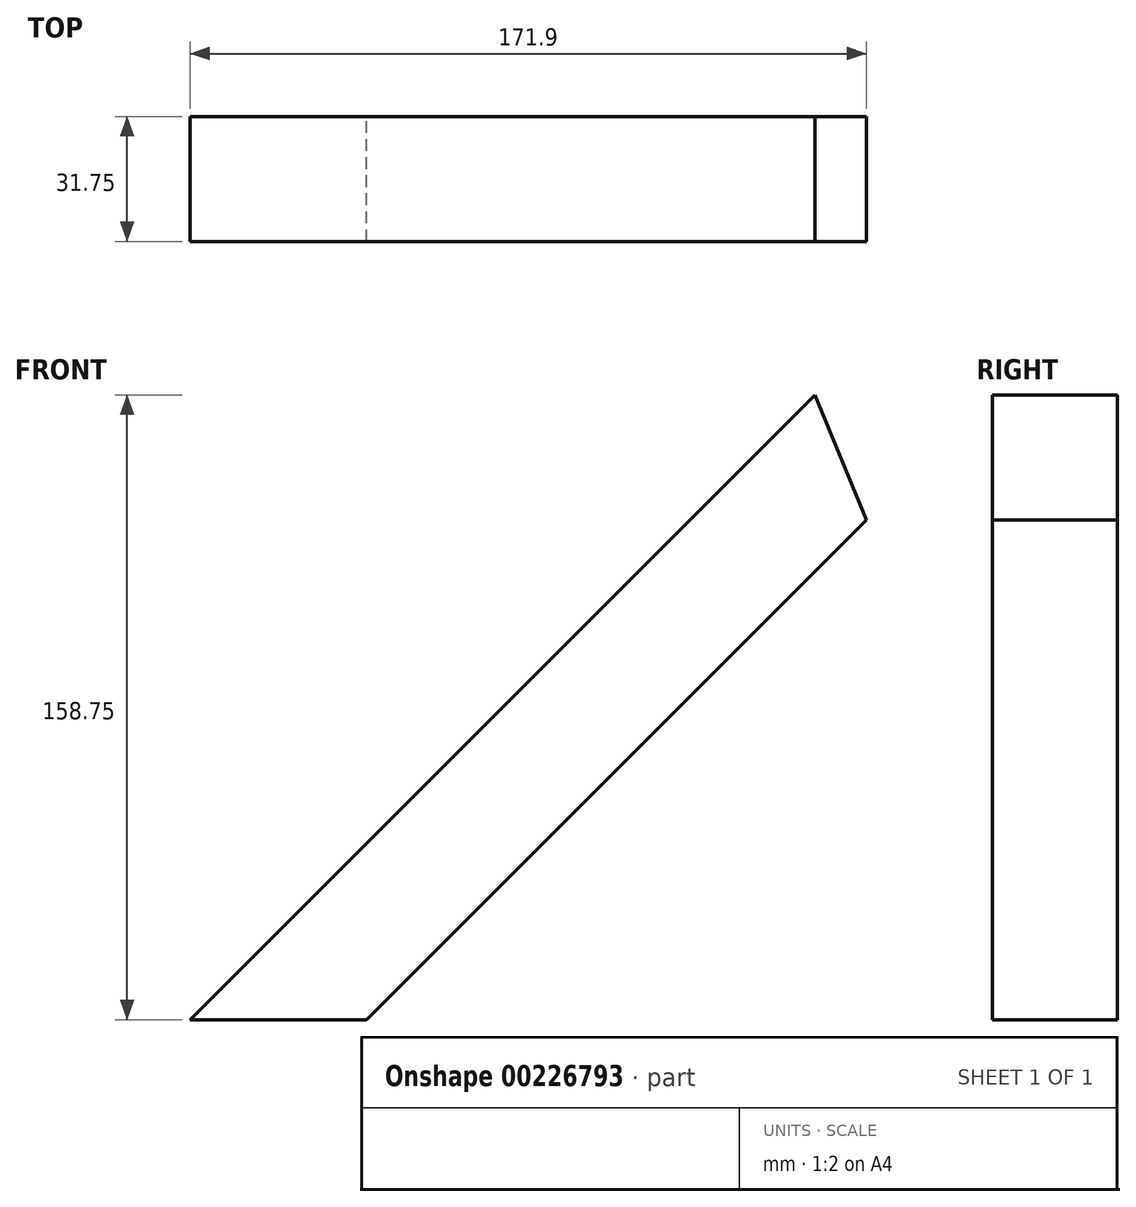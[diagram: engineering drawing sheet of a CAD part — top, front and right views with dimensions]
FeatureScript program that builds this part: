
annotation { "Feature Type Name" : "Feature", "Feature Type Description" : "" }
export const myFeature = defineFeature(function(context is Context, id is Id, definition is map)
    precondition{}
    {
        {
            var Q0;
            Q0=qCreatedBy(makeId("Front.planeOp"),FACE);
            var sketch = newSketch(context, id + "F0", { "sketchPlane" : qUnion([Q0])});
            skLineSegment(sketch, "E0", {"start": v(-93.89, -71.44) * mm, "end": v(64.86, 87.31) * mm});
            skLineSegment(sketch, "E1", {"start": v(78.01, 55.56) * mm, "end": v(-48.99, -71.44) * mm});
            skLineSegment(sketch, "E2", {"start": v(-93.89, -71.44) * mm, "end": v(-48.99, -71.44) * mm});
            skLineSegment(sketch, "E3", {"start": v(64.86, 87.31) * mm, "end": v(78.01, 55.56) * mm});
            skSolve(sketch);
        }
        {
            var Q0;
            Q0=makeQuery(id+"F0.imprint","IMPRINT",FACE,{"disambiguationData":[TD([[makeQuery(id+"F0.imprint","IMPRINT",EDGE,{"derivedFrom":sQuery(id+"F0.wireOp",EDGE,"E0")}),-1.0]])]});
            extrude(context, id + "F1", {"entities" : qUnion([Q0]), "depth" : 31.75 * mm});
        }
    });
